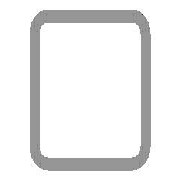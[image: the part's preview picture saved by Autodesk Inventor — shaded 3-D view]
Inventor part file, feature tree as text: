
AUTODESK INVENTOR PART (.ipt)
format: ipt  version: 2025.3 (Build 293356000, 356)  size: 133,632 bytes
history: native  units: mm (DEFAULTED — no unit token found)
features: other x4, sketch x1, plane x1
ambient origin geometry x8: Origin, YZ Plane, XZ Plane, XY Plane, X Axis, Y Axis, Z Axis, Center Point
bodies: Solid1 (feature_tree), Body (feature_tree)
feature tree (6):
  parser-record x1  (decoder bookkeeping rows leaked as tree rows — omitted from the tree; the rows remain in map.json)
  other  "Driven Length"
  other  "Start Plane"
  other  "End Plane"
  sketch  "Sketch3"  dims[d3=1000.0mm d4=0.0mm d7=4.0mm d9=40.0mm d11=40.0mm d12=2.0mm d13=20.0mm d14=1020.0mm d15=20.0mm d16=20.0mm d17=90.0deg d18=1000.0mm]
  plane  "Work Plane3"
